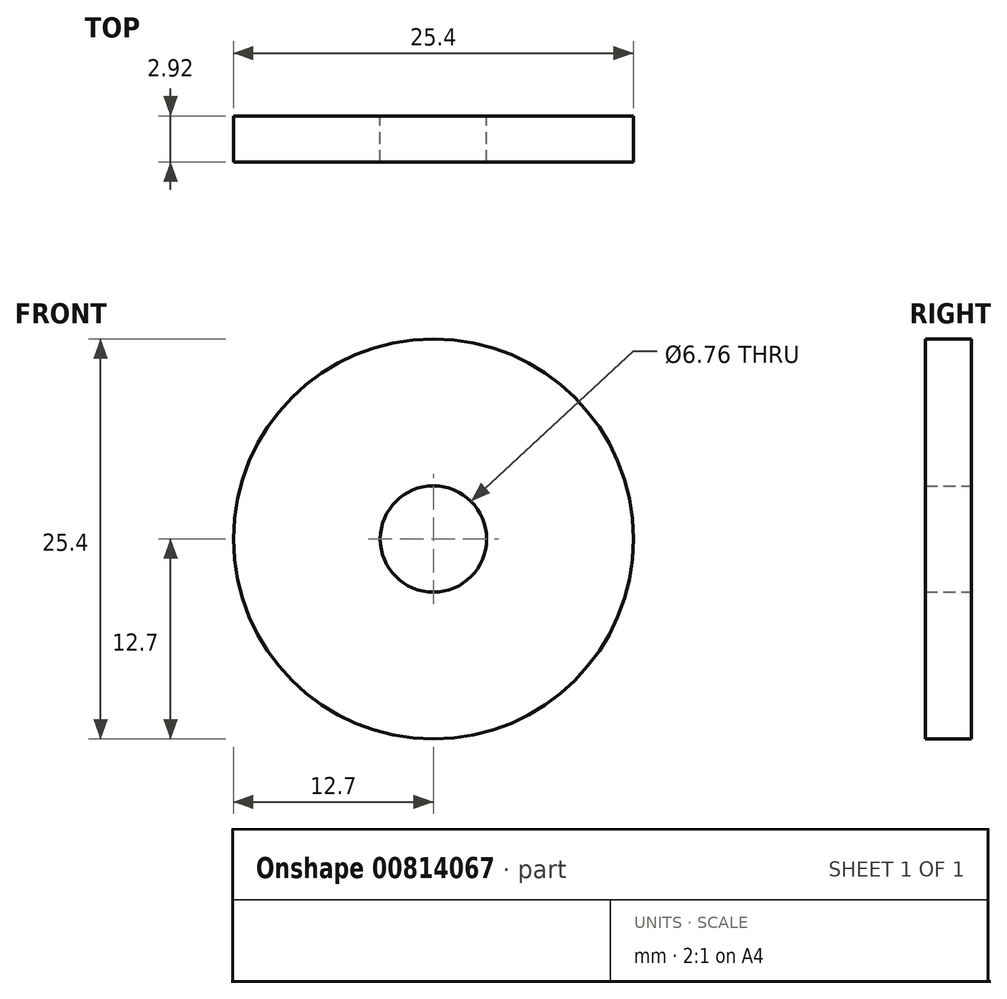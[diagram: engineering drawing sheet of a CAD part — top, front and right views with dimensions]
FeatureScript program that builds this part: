
annotation { "Feature Type Name" : "Feature", "Feature Type Description" : "" }
export const myFeature = defineFeature(function(context is Context, id is Id, definition is map)
    precondition{}
    {
        {
            var Q0;
            Q0=qCreatedBy(makeId("Front.planeOp"),FACE);
            var sketch = newSketch(context, id + "F0", { "sketchPlane" : qUnion([Q0])});
            skCircle(sketch, "E0", {"center": v(0, 0) * mm, "radius": 12.7 * mm});
            skCircle(sketch, "E1", {"center": v(0, 0) * mm, "radius": 3.38 * mm});
            skSolve(sketch);
        }
        {
            var Q0;
            Q0 = qSketchRegion(id + "F0", true);
            extrude(context, id + "F1", {"entities" : qUnion([Q0]), "depth" : 2.92 * mm, "offsetDistance" : 25.4 * mm});
        }
    });
